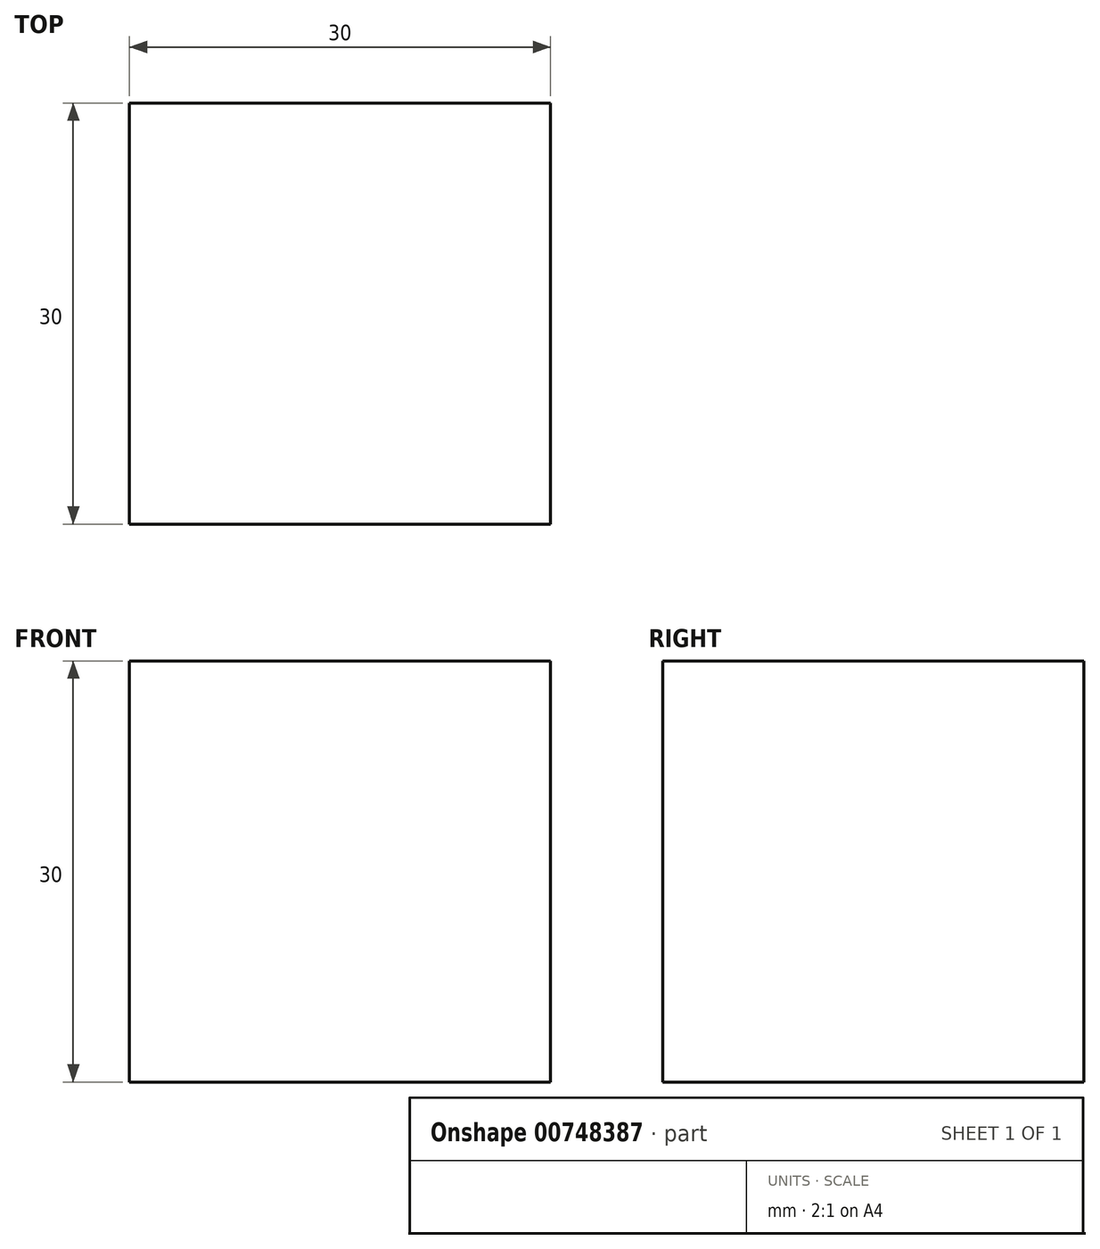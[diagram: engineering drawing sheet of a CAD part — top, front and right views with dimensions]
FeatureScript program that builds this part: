
annotation { "Feature Type Name" : "Feature", "Feature Type Description" : "" }
export const myFeature = defineFeature(function(context is Context, id is Id, definition is map)
    precondition{}
    {
        {
            var Q0;
            Q0=qCreatedBy(makeId("Top.planeOp"),FACE);
            var sketch = newSketch(context, id + "F0", { "sketchPlane" : qUnion([Q0])});
            skLineSegment(sketch, "E0.bottom", {"start": v(0, 0) * mm, "end": v(30, 0) * mm});
            skLineSegment(sketch, "E0.top", {"start": v(0, 30) * mm, "end": v(30, 30) * mm});
            skLineSegment(sketch, "E0.left", {"start": v(0, 0) * mm, "end": v(0, 30) * mm});
            skLineSegment(sketch, "E0.right", {"start": v(30, 0) * mm, "end": v(30, 30) * mm});
            skSolve(sketch);
        }
        {
            var Q0;
            Q0 = qSketchRegion(id + "F0", true);
            extrude(context, id + "F1", {"entities" : qUnion([Q0]), "depth" : 30 * mm, "offsetDistance" : 25 * mm});
        }
    });
